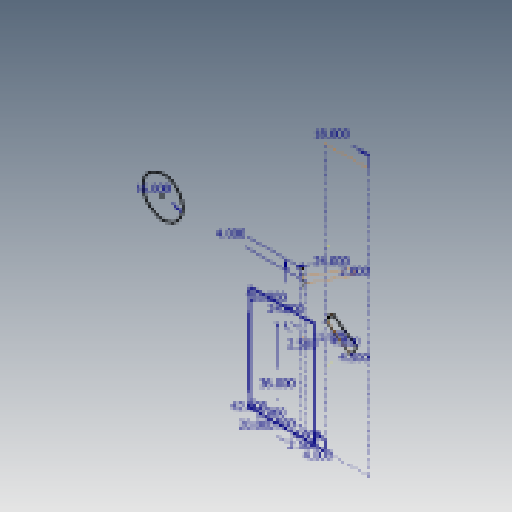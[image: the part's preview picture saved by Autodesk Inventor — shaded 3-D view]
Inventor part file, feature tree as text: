
AUTODESK INVENTOR PART (.ipt)
format: ipt  version: 2023.5 (Build 275446000, 446)  size: 106,496 bytes
history: native  units: in
note: dims shown in document units (in); Inventor stores cm internally (conversion verified against a paired STEP export)
features: other x6, reference x3, sketch x1
ambient origin geometry x8: Origin, YZ Plane, XZ Plane, XY Plane, X Axis, Y Axis, Z Axis, Center Point
feature tree (10):
  sketch  "Sketch1"  dims[d0=26.0in d1=42.0in d2=4.0in d3=4.0in d4=16.0in d5=11.875in d6=4.5in d7=18.0in d8=2.5in d9=36.0in d10=2.0in d11=1.5in d12=2.5in d13=24.0in d14=20.0in d16=2.0in d17=24.0in d18=4.0in d19=4.0in]
  reference  "Reference1"
  reference  "Reference2"
  reference  "Reference3"
  other  "<userpath>\Documents\GitHub\2025-ReefScape---CAD\mock up 1.iam"
  other  "mock up 1.iam"
  other  "TE-25300:1"
  other  "TE-25312_19"
  other  "TE-25312_20"
  other  "TE-25313_9157K765_21"
